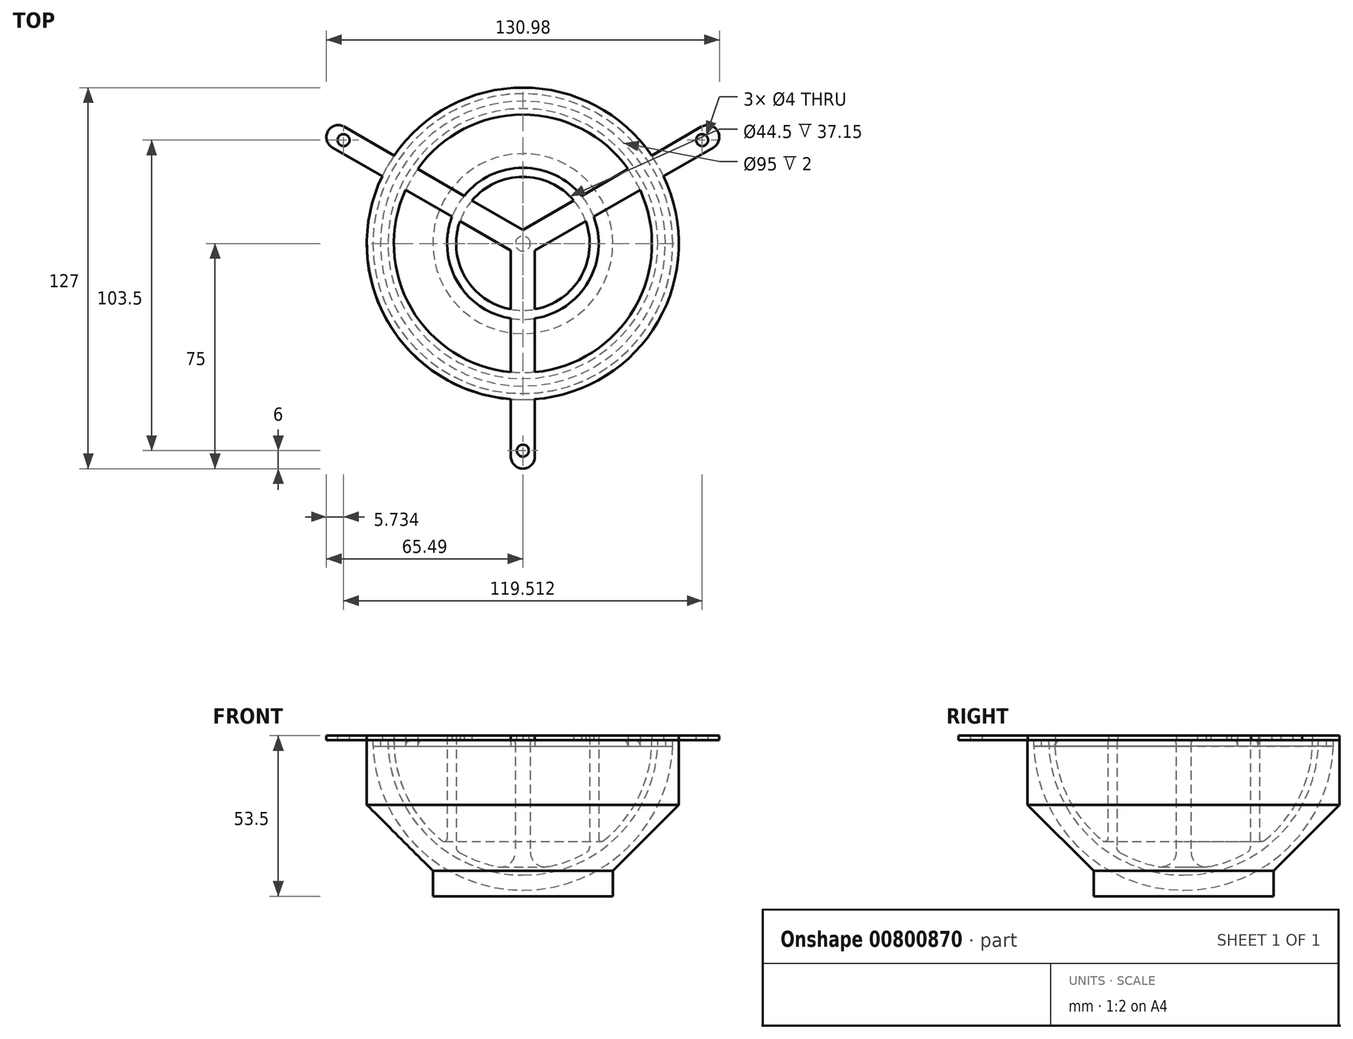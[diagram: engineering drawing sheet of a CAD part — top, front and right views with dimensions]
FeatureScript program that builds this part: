
annotation { "Feature Type Name" : "Feature", "Feature Type Description" : "" }
export const myFeature = defineFeature(function(context is Context, id is Id, definition is map)
    precondition{}
    {
        {
            var Q0;
            Q0=qCreatedBy(makeId("Front.planeOp"),FACE);
            var sketch = newSketch(context, id + "F0", { "sketchPlane" : qUnion([Q0])});
            skLineSegment(sketch, "E0.bottom", {"start": v(0, 0) * mm, "end": v(-52, 0) * mm});
            skLineSegment(sketch, "E0.top", {"start": v(0, 52) * mm, "end": v(-52, 52) * mm});
            skLineSegment(sketch, "E0.left", {"start": v(0, 0) * mm, "end": v(0, 52) * mm});
            skLineSegment(sketch, "E0.right", {"start": v(-52, 0) * mm, "end": v(-52, 52) * mm});
            skArc(sketch, "E1", {"start": v(-50, 52) * mm, "mid": v(-35.36, 16.64) * mm, "end": v(0, 2) * mm});
            skLineSegment(sketch, "E2", {"start": v(-50, 52) * mm, "end": v(-50, 44.7) * mm, "construction": true});
            skLineSegment(sketch, "E3", {"start": v(0, 2) * mm, "end": v(-8.55, 2) * mm, "construction": true});
            skArc(sketch, "E4", {"start": v(-45, 52) * mm, "mid": v(-31.82, 20.18) * mm, "end": v(0, 7) * mm});
            skLineSegment(sketch, "E5", {"start": v(-45, 52) * mm, "end": v(-45, 44.7) * mm, "construction": true});
            skLineSegment(sketch, "E6", {"start": v(0, 7) * mm, "end": v(-8.55, 7) * mm, "construction": true});
            skLineSegment(sketch, "E7", {"start": v(-52, 30.46) * mm, "end": v(-21.54, 0) * mm});
            skPoint(sketch, "E8", {"position": v(-26, 0) * mm});
            skLineSegment(sketch, "E9.bottom", {"start": v(0, 52) * mm, "end": v(-47.5, 52) * mm});
            skLineSegment(sketch, "E9.top", {"start": v(0, 50) * mm, "end": v(-47.5, 50) * mm});
            skLineSegment(sketch, "E9.left", {"start": v(0, 52) * mm, "end": v(0, 50) * mm});
            skLineSegment(sketch, "E9.right", {"start": v(-47.5, 52) * mm, "end": v(-47.5, 50) * mm});
            skLineSegment(sketch, "E10", {"start": v(-30, 0) * mm, "end": v(-30, 8.46) * mm});
            skLineSegment(sketch, "E11.top", {"start": v(0, 53.5) * mm, "end": v(-52, 53.5) * mm});
            skLineSegment(sketch, "E11.left", {"start": v(0, 52) * mm, "end": v(0, 53.5) * mm});
            skLineSegment(sketch, "E11.right", {"start": v(-52, 52) * mm, "end": v(-52, 53.5) * mm});
            skLineSegment(sketch, "E12.bottom", {"start": v(-4, 53.5) * mm, "end": v(4, 53.5) * mm});
            skLineSegment(sketch, "E12.top", {"start": v(-4, 52) * mm, "end": v(4, 52) * mm});
            skLineSegment(sketch, "E12.left", {"start": v(-4, 53.5) * mm, "end": v(-4, 52) * mm});
            skLineSegment(sketch, "E12.right", {"start": v(4, 53.5) * mm, "end": v(4, 52) * mm});
            skArc(sketch, "E13", {"start": v(-43, 52) * mm, "mid": v(-38.76, 33.38) * mm, "end": v(-26.87, 18.43) * mm, "construction": true});
            skLineSegment(sketch, "E14.bottom", {"start": v(0, 50) * mm, "end": v(-2.5, 50) * mm});
            skLineSegment(sketch, "E14.left", {"start": v(0, 50) * mm, "end": v(0, 7.07) * mm});
            skLineSegment(sketch, "E14.right", {"start": v(-2.5, 50) * mm, "end": v(-2.5, 14.75) * mm});
            skArc(sketch, "E15.filletArc", {"start": v(-8.49, 9.85) * mm, "mid": v(-4.33, 10.88) * mm, "end": v(-2.5, 14.75) * mm});
            skLineSegment(sketch, "E16", {"start": v(-23.75, 50) * mm, "end": v(-23.75, 16.15) * mm, "construction": true});
            skLineSegment(sketch, "E17", {"start": v(-25.25, 50) * mm, "end": v(-25.25, 19.21) * mm});
            skLineSegment(sketch, "E18", {"start": v(-22.25, 50) * mm, "end": v(-22.25, 16.35) * mm});
            skArc(sketch, "E19", {"start": v(-43, 52) * mm, "mid": v(-38.3, 32.46) * mm, "end": v(-25.25, 17.2) * mm});
            skArc(sketch, "E20", {"start": v(-21.24, 14.61) * mm, "mid": v(-15.05, 11.72) * mm, "end": v(-8.49, 9.85) * mm});
            skArc(sketch, "E21.filletArc", {"start": v(-26.87, 18.43) * mm, "mid": v(-25.82, 18.31) * mm, "end": v(-25.25, 19.21) * mm});
            skPoint(sketch, "E22.visualSharp", {"position": v(-22.25, 15.2) * mm});
            skArc(sketch, "E22.filletArc", {"start": v(-22.25, 16.35) * mm, "mid": v(-21.98, 15.34) * mm, "end": v(-21.24, 14.61) * mm});
            skLineSegment(sketch, "E23", {"start": v(-25.25, 50) * mm, "end": v(-25.25, 53.5) * mm});
            skLineSegment(sketch, "E24", {"start": v(-22.25, 50) * mm, "end": v(-22.25, 53.5) * mm});
            skLineSegment(sketch, "E25", {"start": v(-43, 52) * mm, "end": v(-43, 53.5) * mm});
            skLineSegment(sketch, "E26", {"start": v(-2.5, 50) * mm, "end": v(-2.5, 52) * mm});
            skLineSegment(sketch, "E27", {"start": v(-2.5, 7.07) * mm, "end": v(-2.5, 2.06) * mm});
            skLineSegment(sketch, "E28", {"start": v(-47.5, 50) * mm, "end": v(-49.96, 50) * mm});
            skSolve(sketch);
        }
        {
            var Q0;
            {var subQ3=sQuery(id+"F0.wireOp",EDGE,"E7");var subQ8=sQuery(id+"F0.wireOp",EDGE,"E0.bottom");var subQ10=makeQuery(id+"F0.imprint","INTERSECT",VERTEX,{"derivedFrom":[subQ8,subQ3]});Q0=makeQuery(id+"F0.imprint","IMPRINT",FACE,{"disambiguationData":[TD([[makeQuery(id+"F0.imprint","IMPRINT",EDGE,{"disambiguationData":[TD([[subQ10,1.0]])],"derivedFrom":subQ8}),-1.0]])]});}
            var Q1;
            {var subQ0=sQuery(id+"F0.wireOp",EDGE,"E10");Q1=makeQuery(id+"F0.imprint","IMPRINT",FACE,{"disambiguationData":[TD([[makeQuery(id+"F0.imprint","IMPRINT",EDGE,{"derivedFrom":subQ0}),-1.0]])]});}
            var Q2;
            Q2=sQuery(id+"F0.wireOp",EDGE,"E0.left");
            revolve(context, id + "F1", {"surfaceOperationType" : NewSurfaceOperationType.NEW, "entities" : qUnion([Q0, Q1]), "axis" : qUnion([Q2]), "revolveType" : RevolveType.FULL});
        }
        {
            var Q0;
            {var subQ9=sQuery(id+"F0.wireOp",EDGE,"E14.right");Q0=makeQuery(id+"F0.imprint","IMPRINT",FACE,{"disambiguationData":[TD([[makeQuery(id+"F0.imprint","IMPRINT",EDGE,{"derivedFrom":subQ9}),1.0]])]});}
            var Q1;
            {var subQ3=sQuery(id+"F0.wireOp",EDGE,"E26");Q1=makeQuery(id+"F0.imprint","IMPRINT",FACE,{"disambiguationData":[TD([[makeQuery(id+"F0.imprint","IMPRINT",EDGE,{"derivedFrom":subQ3}),-1.0]])]});}
            var Q2;
            {var subQ0=sQuery(id+"F0.wireOp",EDGE,"E11.left");Q2=makeQuery(id+"F0.imprint","IMPRINT",FACE,{"disambiguationData":[TD([[makeQuery(id+"F0.imprint","IMPRINT",EDGE,{"derivedFrom":subQ0}),1.0]])]});}
            var Q3;
            {var subQ0=sQuery(id+"F0.wireOp",EDGE,"E24");var subQ1=sQuery(id+"F0.wireOp",EDGE,"E0.top");var subQ2=makeQuery(id+"F0.imprint","INTERSECT",VERTEX,{"derivedFrom":[subQ1,subQ0]});Q3=makeQuery(id+"F0.imprint","IMPRINT",FACE,{"disambiguationData":[TD([[makeQuery(id+"F0.imprint","IMPRINT",EDGE,{"disambiguationData":[TD([[subQ2,-1.0]])],"derivedFrom":subQ1}),1.0]])]});}
            var Q4;
            {var subQ0=sQuery(id+"F0.wireOp",EDGE,"E24");var subQ1=sQuery(id+"F0.wireOp",EDGE,"E0.top");var subQ2=makeQuery(id+"F0.imprint","INTERSECT",VERTEX,{"derivedFrom":[subQ1,subQ0]});Q4=makeQuery(id+"F0.imprint","IMPRINT",FACE,{"disambiguationData":[TD([[makeQuery(id+"F0.imprint","IMPRINT",EDGE,{"disambiguationData":[TD([[subQ2,-1.0]])],"derivedFrom":subQ1}),-1.0]])]});}
            var Q5;
            {var subQ0=sQuery(id+"F0.wireOp",EDGE,"E4");var subQ1=sQuery(id+"F0.wireOp",EDGE,"E0.top");var subQ2=makeQuery(id+"F0.imprint","INTERSECT",VERTEX,{"derivedFrom":[subQ1,subQ0]});Q5=makeQuery(id+"F0.imprint","IMPRINT",FACE,{"disambiguationData":[TD([[makeQuery(id+"F0.imprint","IMPRINT",EDGE,{"disambiguationData":[TD([[subQ2,-1.0]])],"derivedFrom":subQ0}),1.0]])]});}
            var Q6;
            {var subQ0=sQuery(id+"F0.wireOp",EDGE,"E11.right");Q6=makeQuery(id+"F0.imprint","IMPRINT",FACE,{"disambiguationData":[TD([[makeQuery(id+"F0.imprint","IMPRINT",EDGE,{"derivedFrom":subQ0}),-1.0]])]});}
            var Q7;
            {var subQ3=sQuery(id+"F0.wireOp",EDGE,"E9.right");Q7=makeQuery(id+"F0.imprint","IMPRINT",FACE,{"disambiguationData":[TD([[makeQuery(id+"F0.imprint","IMPRINT",EDGE,{"derivedFrom":subQ3}),-1.0]])]});}
            var Q8;
            Q8=sQuery(id+"F0.wireOp",EDGE,"E0.left");
            revolve(context, id + "F2", {"surfaceOperationType" : NewSurfaceOperationType.NEW, "entities" : qUnion([Q0, Q1, Q2, Q3, Q4, Q5, Q6, Q7]), "axis" : qUnion([Q8]), "revolveType" : RevolveType.FULL});
        }
        {
            var Q0;
            Q0=makeQuery(id+"F2.opRevolve","SWEPT_EDGE",EDGE,{"disambiguationData":[OSD([sQuery(id+"F0.wireOp",EDGE,"E0.top"),sQuery(id+"F0.wireOp",EDGE,"E26")])]});
            fillet(context, id + "F3", {"entities" : qUnion([Q0]), "radius" : 1 * mm, "tangentPropagation" : true, "allowEdgeOverflow" : false});
        }
        {
            var Q0;
            Q0=makeQuery(id+"F0.imprint","IMPRINT",FACE,{"disambiguationData":[TD([[makeQuery(id+"F0.imprint","IMPRINT",EDGE,{"derivedFrom":sQuery(id+"F0.wireOp",EDGE,"E11.left")}),-1.0]])]});
            var Q1;
            {var subQ0=sQuery(id+"F0.wireOp",EDGE,"E11.left");Q1=makeQuery(id+"F0.imprint","IMPRINT",FACE,{"disambiguationData":[TD([[makeQuery(id+"F0.imprint","IMPRINT",EDGE,{"derivedFrom":subQ0}),1.0]])]});}
            extrude(context, id + "F4", {"entities" : qUnion([Q0, Q1]), "depth" : 75 * mm, "offsetDistance" : 25 * mm});
        }
        {
            var Q0;
            Q0=makeQuery(id+"F4.opExtrude","SWEPT_FACE",FACE,{"disambiguationData":[OSD([sQuery(id+"F0.wireOp",EDGE,"E11.top"),sQuery(id+"F0.wireOp",EDGE,"E12.bottom")])]});
            var sketch = newSketch(context, id + "F5", { "sketchPlane" : qUnion([Q0])});
            skLineSegment(sketch, "E29.0", {"start": v(-4, -75) * mm, "end": v(-4, 0) * mm});
            skLineSegment(sketch, "E29.1", {"start": v(-4, -75) * mm, "end": v(4, -75) * mm});
            skLineSegment(sketch, "E29.2", {"start": v(4, -75) * mm, "end": v(4, 0) * mm});
            skLineSegment(sketch, "E30", {"start": v(0, -75) * mm, "end": v(0, -65.08) * mm, "construction": true});
            skLineSegment(sketch, "E31", {"start": v(4, -69) * mm, "end": v(-4, -69) * mm, "construction": true});
            skCircle(sketch, "E32", {"center": v(0, -69) * mm, "radius": 2 * mm});
            skSolve(sketch);
        }
        {
            var Q0;
            Q0=makeQuery(id+"F5.imprint","IMPRINT",FACE,{"disambiguationData":[TD([[makeQuery(id+"F5.imprint","IMPRINT",EDGE,{"derivedFrom":sQuery(id+"F5.wireOp",EDGE,"E32")}),1.0]])]});
            extrude(context, id + "F6", {"entities" : qUnion([Q0]), "operationType" : NewBodyOperationType.REMOVE, "endBound" : BoundingType.UP_TO_NEXT, "oppositeDirection" : true, "depth" : 25 * mm, "offsetDistance" : 25 * mm});
        }
        {
            var Q0;
            Q0=makeQuery(id+"F4.opExtrude","CAP_EDGE",EDGE,{"disambiguationData":[OSD([sQuery(id+"F0.wireOp",EDGE,"E12.right")])],"isStart":false});
            var Q1;
            Q1=makeQuery(id+"F4.opExtrude","CAP_EDGE",EDGE,{"disambiguationData":[OSD([sQuery(id+"F0.wireOp",EDGE,"E12.left")])],"isStart":false});
            fillet(context, id + "F7", {"entities" : qUnion([Q0, Q1]), "radius" : 4 * mm, "tangentPropagation" : true, "allowEdgeOverflow" : false});
        }
        {
            var Q0;
            Q0=makeQuery(id+"F4.opExtrude","SWEPT_BODY",BODY,{"disambiguationData":[OSD([sQuery(id+"F0.wireOp",EDGE,"E0.top"),sQuery(id+"F0.wireOp",EDGE,"E11.top"),sQuery(id+"F0.wireOp",EDGE,"E12.bottom"),sQuery(id+"F0.wireOp",EDGE,"E12.top"),sQuery(id+"F0.wireOp",EDGE,"E12.left"),sQuery(id+"F0.wireOp",EDGE,"E12.right")])]});
            var Q1;
            Q1=sQuery(id+"F0.wireOp",EDGE,"E0.left");
            circularPattern(context, id + "F8", {"entities" : qUnion([Q0]), "axis" : qUnion([Q1]), "angle" : 360 * degree, "instanceCount" : 3, "equalSpace" : true});
        }
        {
            var Q0;
            Q0=makeQuery(id+"F2.opRevolve","SWEPT_BODY",BODY,{"disambiguationData":[OSD([sQuery(id+"F0.wireOp",EDGE,"E0.top"),sQuery(id+"F0.wireOp",EDGE,"E0.left"),sQuery(id+"F0.wireOp",EDGE,"E1"),sQuery(id+"F0.wireOp",EDGE,"E4"),sQuery(id+"F0.wireOp",EDGE,"E9.right"),sQuery(id+"F0.wireOp",EDGE,"E11.top"),sQuery(id+"F0.wireOp",EDGE,"E11.left"),sQuery(id+"F0.wireOp",EDGE,"E11.right"),sQuery(id+"F0.wireOp",EDGE,"E12.left"),sQuery(id+"F0.wireOp",EDGE,"E14.right"),sQuery(id+"F0.wireOp",EDGE,"E15.filletArc"),sQuery(id+"F0.wireOp",EDGE,"E17"),sQuery(id+"F0.wireOp",EDGE,"E18"),sQuery(id+"F0.wireOp",EDGE,"E19"),sQuery(id+"F0.wireOp",EDGE,"E20"),sQuery(id+"F0.wireOp",EDGE,"E21.filletArc"),sQuery(id+"F0.wireOp",EDGE,"E22.filletArc"),sQuery(id+"F0.wireOp",EDGE,"E23"),sQuery(id+"F0.wireOp",EDGE,"E24"),sQuery(id+"F0.wireOp",EDGE,"E25"),sQuery(id+"F0.wireOp",EDGE,"E26"),sQuery(id+"F0.wireOp",EDGE,"E28")])]});
            var Q1;
            Q1=makeQuery(id+"F4.opExtrude","SWEPT_BODY",BODY,{"disambiguationData":[OSD([sQuery(id+"F0.wireOp",EDGE,"E0.top"),sQuery(id+"F0.wireOp",EDGE,"E11.top"),sQuery(id+"F0.wireOp",EDGE,"E12.bottom"),sQuery(id+"F0.wireOp",EDGE,"E12.top"),sQuery(id+"F0.wireOp",EDGE,"E12.left"),sQuery(id+"F0.wireOp",EDGE,"E12.right")])]});
            var Q2;
            Q2=makeQuery(id+"F8.opPattern","COPY",BODY,{"derivedFrom":makeQuery(id+"F4.opExtrude","SWEPT_BODY",BODY,{"disambiguationData":[OSD([sQuery(id+"F0.wireOp",EDGE,"E0.top"),sQuery(id+"F0.wireOp",EDGE,"E11.top"),sQuery(id+"F0.wireOp",EDGE,"E12.bottom"),sQuery(id+"F0.wireOp",EDGE,"E12.top"),sQuery(id+"F0.wireOp",EDGE,"E12.left"),sQuery(id+"F0.wireOp",EDGE,"E12.right")])]}),"instanceName":"2"});
            var Q3;
            Q3=makeQuery(id+"F8.opPattern","COPY",BODY,{"derivedFrom":makeQuery(id+"F4.opExtrude","SWEPT_BODY",BODY,{"disambiguationData":[OSD([sQuery(id+"F0.wireOp",EDGE,"E0.top"),sQuery(id+"F0.wireOp",EDGE,"E11.top"),sQuery(id+"F0.wireOp",EDGE,"E12.bottom"),sQuery(id+"F0.wireOp",EDGE,"E12.top"),sQuery(id+"F0.wireOp",EDGE,"E12.left"),sQuery(id+"F0.wireOp",EDGE,"E12.right")])]}),"instanceName":"1"});
            var Q4;
            Q4=makeQuery(id+"F2.opRevolve","SWEPT_BODY",BODY,{"disambiguationData":[OSD([sQuery(id+"F0.wireOp",EDGE,"E0.top"),sQuery(id+"F0.wireOp",EDGE,"E0.left"),sQuery(id+"F0.wireOp",EDGE,"E1"),sQuery(id+"F0.wireOp",EDGE,"E4"),sQuery(id+"F0.wireOp",EDGE,"E9.right"),sQuery(id+"F0.wireOp",EDGE,"E11.top"),sQuery(id+"F0.wireOp",EDGE,"E11.left"),sQuery(id+"F0.wireOp",EDGE,"E11.right"),sQuery(id+"F0.wireOp",EDGE,"E12.left"),sQuery(id+"F0.wireOp",EDGE,"E14.right"),sQuery(id+"F0.wireOp",EDGE,"E15.filletArc"),sQuery(id+"F0.wireOp",EDGE,"E17"),sQuery(id+"F0.wireOp",EDGE,"E18"),sQuery(id+"F0.wireOp",EDGE,"E19"),sQuery(id+"F0.wireOp",EDGE,"E20"),sQuery(id+"F0.wireOp",EDGE,"E21.filletArc"),sQuery(id+"F0.wireOp",EDGE,"E22.filletArc"),sQuery(id+"F0.wireOp",EDGE,"E23"),sQuery(id+"F0.wireOp",EDGE,"E24"),sQuery(id+"F0.wireOp",EDGE,"E25"),sQuery(id+"F0.wireOp",EDGE,"E26"),sQuery(id+"F0.wireOp",EDGE,"E28")])]});
            booleanBodies(context, id + "F9", {"operationType" : BooleanOperationType.UNION, "tools" : qUnion([Q0, Q1, Q2, Q3, Q4])});
        }
        {
            var Q0;
            Q0=makeQuery(id+"F9.opBoolean","INTERSECT",EDGE,{"disambiguationData":[OD(0.0)],"derivedFrom":[makeQuery(id+"F2.opRevolve","SWEPT_FACE",FACE,{"disambiguationData":[OSD([sQuery(id+"F0.wireOp",EDGE,"E18"),sQuery(id+"F0.wireOp",EDGE,"E24")])]}),makeQuery(id+"F8.opPattern","COPY",FACE,{"derivedFrom":makeQuery(id+"F4.opExtrude","SWEPT_FACE",FACE,{"disambiguationData":[OSD([sQuery(id+"F0.wireOp",EDGE,"E0.top"),sQuery(id+"F0.wireOp",EDGE,"E12.top")])]}),"instanceName":"1"})]});
            var Q1;
            Q1=makeQuery(id+"F9.opBoolean","INTERSECT",EDGE,{"disambiguationData":[OD(0.0)],"derivedFrom":[makeQuery(id+"F2.opRevolve","SWEPT_FACE",FACE,{"disambiguationData":[OSD([sQuery(id+"F0.wireOp",EDGE,"E17"),sQuery(id+"F0.wireOp",EDGE,"E23")])]}),makeQuery(id+"F8.opPattern","COPY",FACE,{"derivedFrom":makeQuery(id+"F4.opExtrude","SWEPT_FACE",FACE,{"disambiguationData":[OSD([sQuery(id+"F0.wireOp",EDGE,"E0.top"),sQuery(id+"F0.wireOp",EDGE,"E12.top")])]}),"instanceName":"1"})]});
            var Q2;
            {var subQ0=sQuery(id+"F0.wireOp",EDGE,"E0.top");var subQ1=makeQuery(id+"F4.opExtrude","SWEPT_FACE",FACE,{"disambiguationData":[OSD([subQ0,sQuery(id+"F0.wireOp",EDGE,"E12.top")])]});var subQ2=sQuery(id+"F0.wireOp",EDGE,"E25");var subQ3=sQuery(id+"F0.wireOp",EDGE,"E19");var subQ4=makeQuery(id+"F2.opRevolve","SWEPT_FACE",FACE,{"disambiguationData":[OSD([subQ3])]});var subQ5=subQ1;var subQ6=makeQuery(id+"F8.opPattern","COPY",FACE,{"derivedFrom":subQ5,"instanceName":"1"});var subQ7=makeQuery(id+"F8.opPattern","COPY",FACE,{"derivedFrom":subQ5,"instanceName":"2"});Q2=makeQuery(id+"F9.opBoolean","SPLIT",EDGE,{"disambiguationData":[topologyDisambiguationEdgeConnected([subQ4,subQ1,subQ6,subQ7]),TD([makeQuery(id+"F4.opExtrude","SWEPT_FACE",FACE,{"disambiguationData":[OSD([sQuery(id+"F0.wireOp",EDGE,"E12.left")])]})])],"derivedFrom":makeQuery(id+"F2.opRevolve","SWEPT_EDGE",EDGE,{"disambiguationData":[OSD([subQ0,subQ3,subQ2])]})});}
            var Q3;
            Q3=makeQuery(id+"F9.opBoolean","INTERSECT",EDGE,{"disambiguationData":[OD(2.0)],"derivedFrom":[makeQuery(id+"F2.opRevolve","SWEPT_FACE",FACE,{"disambiguationData":[OSD([sQuery(id+"F0.wireOp",EDGE,"E18"),sQuery(id+"F0.wireOp",EDGE,"E24")])]}),makeQuery(id+"F8.opPattern","COPY",FACE,{"derivedFrom":makeQuery(id+"F4.opExtrude","SWEPT_FACE",FACE,{"disambiguationData":[OSD([sQuery(id+"F0.wireOp",EDGE,"E0.top"),sQuery(id+"F0.wireOp",EDGE,"E12.top")])]}),"instanceName":"1"})]});
            var Q4;
            Q4=makeQuery(id+"F9.opBoolean","INTERSECT",EDGE,{"disambiguationData":[OD(2.0)],"derivedFrom":[makeQuery(id+"F2.opRevolve","SWEPT_FACE",FACE,{"disambiguationData":[OSD([sQuery(id+"F0.wireOp",EDGE,"E17"),sQuery(id+"F0.wireOp",EDGE,"E23")])]}),makeQuery(id+"F8.opPattern","COPY",FACE,{"derivedFrom":makeQuery(id+"F4.opExtrude","SWEPT_FACE",FACE,{"disambiguationData":[OSD([sQuery(id+"F0.wireOp",EDGE,"E0.top"),sQuery(id+"F0.wireOp",EDGE,"E12.top")])]}),"instanceName":"1"})]});
            var Q5;
            {var subQ0=sQuery(id+"F0.wireOp",EDGE,"E0.top");var subQ1=makeQuery(id+"F4.opExtrude","SWEPT_FACE",FACE,{"disambiguationData":[OSD([subQ0,sQuery(id+"F0.wireOp",EDGE,"E12.top")])]});var subQ2=subQ1;var subQ3=makeQuery(id+"F8.opPattern","COPY",FACE,{"derivedFrom":subQ2,"instanceName":"1"});var subQ4=sQuery(id+"F0.wireOp",EDGE,"E19");var subQ5=makeQuery(id+"F2.opRevolve","SWEPT_FACE",FACE,{"disambiguationData":[OSD([subQ4])]});var subQ6=sQuery(id+"F0.wireOp",EDGE,"E25");var subQ7=makeQuery(id+"F8.opPattern","COPY",FACE,{"derivedFrom":subQ2,"instanceName":"2"});Q5=makeQuery(id+"F9.opBoolean","SPLIT",EDGE,{"disambiguationData":[topologyDisambiguationEdgeConnected([subQ5,subQ1,subQ3,subQ7]),TD([makeQuery(id+"F8.opPattern","COPY",FACE,{"derivedFrom":makeQuery(id+"F4.opExtrude","SWEPT_FACE",FACE,{"disambiguationData":[OSD([sQuery(id+"F0.wireOp",EDGE,"E12.left")])]}),"instanceName":"2"})])],"derivedFrom":makeQuery(id+"F2.opRevolve","SWEPT_EDGE",EDGE,{"disambiguationData":[OSD([subQ0,subQ4,subQ6])]})});}
            var Q6;
            Q6=makeQuery(id+"F9.opBoolean","INTERSECT",EDGE,{"disambiguationData":[OD(1.0)],"derivedFrom":[makeQuery(id+"F2.opRevolve","SWEPT_FACE",FACE,{"disambiguationData":[OSD([sQuery(id+"F0.wireOp",EDGE,"E18"),sQuery(id+"F0.wireOp",EDGE,"E24")])]}),makeQuery(id+"F8.opPattern","COPY",FACE,{"derivedFrom":makeQuery(id+"F4.opExtrude","SWEPT_FACE",FACE,{"disambiguationData":[OSD([sQuery(id+"F0.wireOp",EDGE,"E0.top"),sQuery(id+"F0.wireOp",EDGE,"E12.top")])]}),"instanceName":"1"})]});
            var Q7;
            Q7=makeQuery(id+"F9.opBoolean","INTERSECT",EDGE,{"disambiguationData":[OD(1.0)],"derivedFrom":[makeQuery(id+"F2.opRevolve","SWEPT_FACE",FACE,{"disambiguationData":[OSD([sQuery(id+"F0.wireOp",EDGE,"E17"),sQuery(id+"F0.wireOp",EDGE,"E23")])]}),makeQuery(id+"F8.opPattern","COPY",FACE,{"derivedFrom":makeQuery(id+"F4.opExtrude","SWEPT_FACE",FACE,{"disambiguationData":[OSD([sQuery(id+"F0.wireOp",EDGE,"E0.top"),sQuery(id+"F0.wireOp",EDGE,"E12.top")])]}),"instanceName":"1"})]});
            var Q8;
            {var subQ0=sQuery(id+"F0.wireOp",EDGE,"E0.top");var subQ1=makeQuery(id+"F4.opExtrude","SWEPT_FACE",FACE,{"disambiguationData":[OSD([subQ0,sQuery(id+"F0.wireOp",EDGE,"E12.top")])]});var subQ2=sQuery(id+"F0.wireOp",EDGE,"E25");var subQ3=sQuery(id+"F0.wireOp",EDGE,"E19");var subQ4=makeQuery(id+"F2.opRevolve","SWEPT_FACE",FACE,{"disambiguationData":[OSD([subQ3])]});var subQ5=subQ1;var subQ6=makeQuery(id+"F8.opPattern","COPY",FACE,{"derivedFrom":subQ5,"instanceName":"1"});var subQ7=makeQuery(id+"F8.opPattern","COPY",FACE,{"derivedFrom":subQ5,"instanceName":"2"});Q8=makeQuery(id+"F9.opBoolean","SPLIT",EDGE,{"disambiguationData":[topologyDisambiguationEdgeConnected([subQ4,subQ1,subQ6,subQ7]),TD([makeQuery(id+"F8.opPattern","COPY",FACE,{"derivedFrom":makeQuery(id+"F4.opExtrude","SWEPT_FACE",FACE,{"disambiguationData":[OSD([sQuery(id+"F0.wireOp",EDGE,"E12.left")])]}),"instanceName":"1"})])],"derivedFrom":makeQuery(id+"F2.opRevolve","SWEPT_EDGE",EDGE,{"disambiguationData":[OSD([subQ0,subQ3,subQ2])]})});}
            fillet(context, id + "F10", {"entities" : qUnion([Q0, Q1, Q2, Q3, Q4, Q5, Q6, Q7, Q8]), "radius" : 2 * mm, "tangentPropagation" : true, "allowEdgeOverflow" : false});
        }
    });
